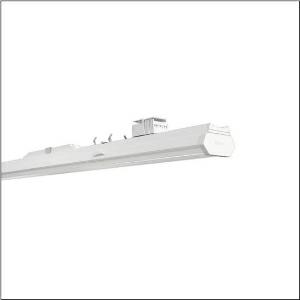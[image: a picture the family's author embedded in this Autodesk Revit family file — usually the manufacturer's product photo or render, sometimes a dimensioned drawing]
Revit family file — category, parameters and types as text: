
# Revit family: licross_21_protected_ho_52td1bcn4b5m
name_source: partatom
category: Lighting Fixtures
units: mm (PartAtom-declared; Revit-internal decimal feet)

## family parameters
Cut with Voids When Loaded = No
Host = Face
Light Source = No
Part Type = Normal
Room Calculation Point = No
Round Connector Dimension = Use Diameter
Shared = No

## types (1)
- --- (1 x LED, 11820 lm, 68.9 W, 4000K)
    Apparent Load = 69 VA
    CIE Flux Codes = 54 82 95 97 100
    Color Rendering = 80
    Color Temperature = 4000K
    Default Elevation = 1800 mm
    Description = Licross 21 Protected HO, luminaire insert, of sheet steel, galvanised, coil coated, white, length: 1.500mm, width: 90mm, height: 103mm, LED rated luminous flux: 11.830lm, light colour: 840, SDCM (Standard Deviation of Colour Matching)MacAdam ≤ 3 SDCM (initial), control gear: ON/OFF Multilumen, CLOi, with plug, 3-pole, with phase selection, mains connection: 220..240V, AC, 50/60Hz, start of lifetime: 69W, end of service life: 83W, internal wiring halogen-free, primary optical cover: cover, of PMMA, light emission: direct distribution, primary light characteristic: symmetric, protection rating (complete): IP54, insulation class (complete): insulation class I (protective earthing), certification: CE, ENEC, VDE, UKCA, protection symbol: D if used in an environment with non-conductive dust loads with corresponding accessories, impact resistance: IK06, permissible ambient temperature for indoor applications: -35..+35°C, corresponds to IFS (International Featured Standards) requirements for safety and quality in the food industry, reducing of maximum allowable ambient temperature of 5°C with ceiling mounting, LABS conformity tested according to VDMA 24364:2018-05, The light source and the operating device comply with the requirements of the Ecodesign Regulation (EU) 2019/2020 and are replaceable in accordance with this regulation, packaging unit: 1 piece
    Height = 92 mm
    Lamp = 1 x LED
    Lamp Light Flux = 11820 lm
    Lamp Power = 68.9 W
    Lamp count = 1
    Length = 1500 mm
    Luminous efficacy = 172 lm/W
    Manufacturer = Siteco
    ModVariant = No
    Model = 52TD1BCN4B5M
    Mounting Place = Ceiling
    Mounting Type = Pendant
    Number of Poles = 1
    OnlyDefault = Yes
    Power Factor = 1
    Product Name = Licross 21 Protected HO
    Product group = luminaire insert | ceiling pendant
    ProductGroupID = 901
    Protection Class = Protection class I
    Protection Degree = IP 54
    RLX_Detail_Level = 1
    RLX_Emergency_Light_Flux = 0 lm
    RLX_Emergency_Type = 0
    RLX_Emergency_Type_DB = No
    RlxData = <blob elided: 22265 chars, md5=906ae66f>
    Socket = socket
    Standby Power = 0 W
    System Light Flux = 11820 lm
    System Power = 69 W
    Type Comments = factory setting: luminous flux: 100 % | (A | C | E) | 162 mA
    Type Image = l_1256148.jpg
    URL = http://relux.com
    VarID = @adj_111481
    Voltage = 0 V
    Weight = 0.00 kg
    Width = 88 mm

## geometry (parser evidence)
native form markers: Blend x4, Sweep x11
no freeform markers — native parametric forms only
